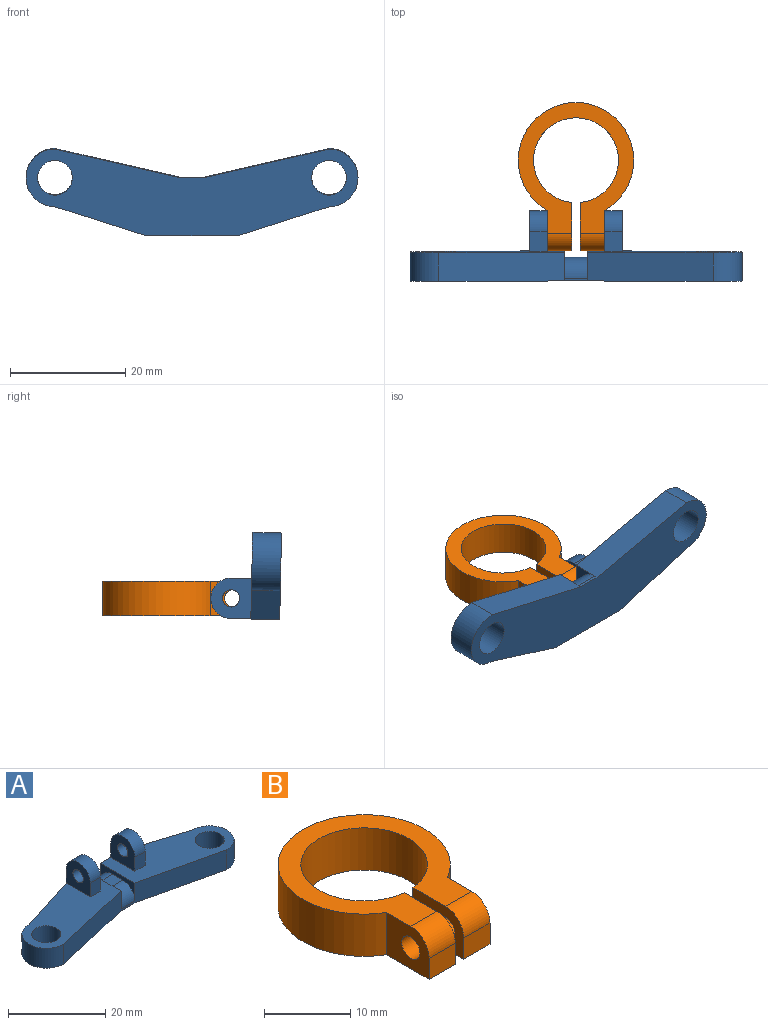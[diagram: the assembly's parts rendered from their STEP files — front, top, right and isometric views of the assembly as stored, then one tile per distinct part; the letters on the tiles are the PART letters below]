
ASSEMBLY  parts=2 mates=1
PART A: 28 faces, bbox 57.5x15x12 mm
  f0: plane 10x4.5mm, normal (1,0,0), area 15.3mm2, adj f4,f6,f9,f11,f13,f14
  f1: plane 7x7mm, normal (-1,0,0), area 36.7mm2, adj f2,f4,f9,f15,f27
  f2: plane 3.5x3mm, normal (0,-1,0), area 10.5mm2, adj f1,f3,f9,f15
  f3: plane 7x7mm, normal (1,0,0), area 36.7mm2, adj f2,f4,f9,f15,f27
  f4: plane 16x8.5mm, normal (0,1,0), area 83mm2, adj f0,f1,f3,f5,f8,f9,f13,f15
  f5: plane 57.5x15mm, normal (0,0,-1), area 527mm2, adj f4,f6,f7,f8,f10,f12,f20,f21
  f6: plane 21.75x5mm, normal (0.22,-0.97,0), area 111.6mm2, adj f0,f5,f9,f10,f12
  f7: cylinder r=3mm len=6mm, axis (0,0,-1), area 94.2mm2, adj f5,f9
  f8: plane 15.75x5mm, normal (-0.3,0.95,0), area 82.6mm2, adj f4,f5,f9,f12
  f9: plane 26.75x15mm, normal (0,0,1), area 222.5mm2, adj f0,f1,f2,f3,f4,f6,f7,f8
  f10: plane 4x0.5mm, normal (0,-1,0), area 2mm2, adj f5,f6,f14,f20
  f11: plane 4x3mm, normal (0,0,1), area 12mm2, adj f0,f13,f14,f16
  f12: cylinder r=5mm len=10mm, axis (0,0,-1), area 78.5mm2, adj f5,f6,f8,f9
  f13: cylinder r=3.5mm len=4mm, axis (1,0,0), area 22mm2, adj f0,f4,f11,f16
  f14: cylinder r=3.5mm len=4mm, axis (-1,0,0), area 22mm2, adj f0,f10,f11,f16
  f15: cylinder r=3.5mm len=7mm, axis (1,0,0), area 33mm2, adj f1,f2,f3,f4
  f16: plane 10x4.5mm, normal (-1,0,0), area 15.3mm2, adj f4,f11,f13,f14,f20,f23
  f17: plane 7x7mm, normal (1,0,0), area 36.7mm2, adj f4,f18,f23,f25,f26
  f18: plane 3.5x3mm, normal (0,-1,0), area 10.5mm2, adj f17,f19,f23,f25
  f19: plane 7x7mm, normal (-1,0,0), area 36.7mm2, adj f4,f18,f23,f25,f26
  f20: plane 21.75x5mm, normal (-0.22,-0.97,0), area 111.6mm2, adj f5,f10,f16,f23,f24
  f21: cylinder r=3mm len=6mm, axis (0,0,-1), area 94.2mm2, adj f5,f23
  f22: plane 15.75x5mm, normal (0.3,0.95,0), area 82.6mm2, adj f4,f5,f23,f24
  f23: plane 26.75x15mm, normal (0,0,1), area 222.5mm2, adj f4,f16,f17,f18,f19,f20,f21,f22
  f24: cylinder r=5mm len=10mm, axis (0,0,-1), area 78.5mm2, adj f5,f20,f22,f23
  f25: cylinder r=3.5mm len=7mm, axis (-1,0,0), area 33mm2, adj f4,f17,f18,f19
  f26: cylinder r=1.5mm len=3mm, axis (-1,0,0), area 28.3mm2, adj f17,f19
  f27: cylinder r=1.5mm len=3mm, axis (-1,0,0), area 28.3mm2, adj f1,f3
PART B: 14 faces, bbox 20x25.7x6 mm
  f0: plane 7x6mm, normal (1,0,0), area 33mm2, adj f1,f7,f8,f9,f10,f13
  f1: cylinder r=10mm len=20mm, axis (0,0,-1), area 314.2mm2, adj f0,f2,f8,f9
  f2: plane 7x6mm, normal (-1,0,0), area 33mm2, adj f1,f3,f8,f9,f11,f12
  f3: plane 4.3x3mm, normal (0,-1,0), area 12.9mm2, adj f2,f4,f9,f12
  f4: plane 8.34x6mm, normal (1,0,0), area 41.1mm2, adj f3,f5,f8,f9,f11,f12
  f5: cylinder r=7.35mm len=14.7mm, axis (0,0,-1), area 268.7mm2, adj f4,f6,f8,f9
  f6: plane 8.34x6mm, normal (-1,0,0), area 41.1mm2, adj f5,f7,f8,f9,f10,f13
  f7: plane 4.3x3mm, normal (0,-1,0), area 12.9mm2, adj f0,f6,f9,f13
  f8: plane 22.66x20mm, normal (0,0,1), area 167.9mm2, adj f0,f1,f2,f4,f5,f6,f12,f13
  f9: plane 25.66x20mm, normal (0,0,-1), area 193.7mm2, adj f0,f1,f2,f3,f4,f5,f6,f7
  f10: cylinder r=1.5mm len=4.3mm, axis (1,0,0), area 40.5mm2, adj f0,f6
  f11: cylinder r=1.5mm len=4.3mm, axis (1,0,0), area 40.5mm2, adj f2,f4
  f12: cylinder r=3mm len=4.3mm, axis (-1,0,0), area 20.3mm2, adj f2,f3,f4,f8
  f13: cylinder r=3mm len=4.3mm, axis (-1,0,0), area 20.3mm2, adj f0,f6,f7,f8
PLACE A rot(axis=(-1,0,0),88.8deg) t=(-117.07,-23.68,3.09)mm
PLACE B t=(-51.54,-20.62,-11.23)mm
MATE revolute A.f19 <-> B.f12  axis (-1,0,0) through (-77.98,-15.33,-8.23)mm
